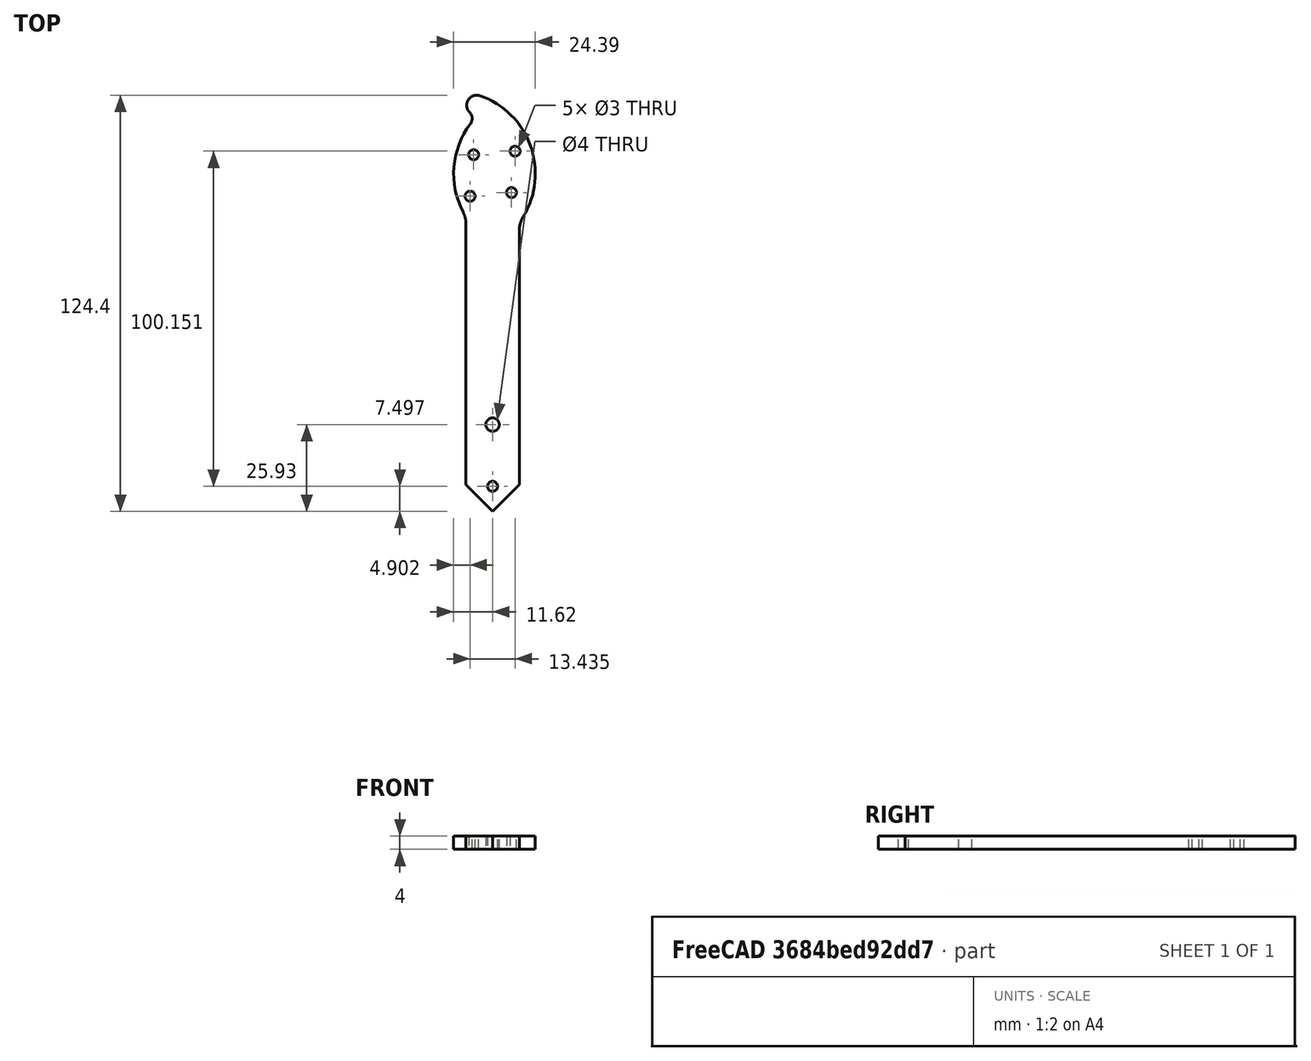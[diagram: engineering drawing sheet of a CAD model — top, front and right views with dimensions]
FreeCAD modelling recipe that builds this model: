
FCSTD DOCUMENT  (FreeCAD 0.18RUnknown)
Label: arm_left
License: All rights reserved
LicenseURL: http://en.wikipedia.org/wiki/All_rights_reserved
objects: Sketcher::SketchObject×1, Part::Extrusion×1, App::Part×1
note: 2 computed .brp shape members not serialized (recipe doc carries the construction recipe); baked Part::Feature solids carry a one-line shape summary decoded from their .brp

FEATURE [Sketcher::SketchObject] Sketch002
  expr: Constraints[9] = anomaly#Spreadsheet.armLength
  expr: Constraints[20] = anomaly#Spreadsheet.armOffsetElectro
  expr: Constraints[10] = anomaly#Spreadsheet.armHoleCenterOffset
  sketch-geometry (24):
    g0: LineSegment StartX=-8 StartY=-92.9332 StartZ=0 EndX=-8 EndY=-17.0009 EndZ=0
    g1: ArcOfCircle CenterX=-16 CenterY=-17.0009 CenterZ=0 NormalX=0 NormalY=0 NormalZ=1 AngleXU=0 Radius=8 StartAngle=-1.039e-13 EndAngle=0.546741
    g2: ArcOfCircle CenterX=15 CenterY=-14.7043 CenterZ=0 NormalX=0 NormalY=0 NormalZ=1 AngleXU=0 Radius=7 StartAngle=2.65925 EndAngle=3.14159
    g3: Circle [constr] CenterX=0 CenterY=0 CenterZ=0 NormalX=0 NormalY=0 NormalZ=1 AngleXU=0 Radius=8
    g4: Circle [constr] CenterX=0 CenterY=0 CenterZ=0 NormalX=0 NormalY=0 NormalZ=1 AngleXU=0 Radius=9.5
    g5: LineSegment [constr] StartX=-6.71751 StartY=6.71751 StartZ=0 EndX=6.71751 EndY=-6.71751 EndZ=0
    g6: LineSegment [constr] StartX=-5.65685 StartY=-5.65685 StartZ=0 EndX=5.65685 EndY=5.65685 EndZ=0
    g7: Circle CenterX=0 CenterY=-75 CenterZ=0 NormalX=0 NormalY=0 NormalZ=1 AngleXU=0 Radius=2
    g8: ArcOfCircle CenterX=11.9331 CenterY=0 CenterZ=0 NormalX=0 NormalY=0 NormalZ=1 AngleXU=0 Radius=24.7 StartAngle=1.90923 EndAngle=3.68833
    g9: ArcOfCircle CenterX=4.72855 CenterY=20.4691 CenterZ=0 NormalX=0 NormalY=0 NormalZ=1 AngleXU=0 Radius=3 StartAngle=5.51344 EndAngle=8.19241
    g10: ArcOfCircle CenterX=8.84318 CenterY=16.4813 CenterZ=0 NormalX=0 NormalY=0 NormalZ=1 AngleXU=0 Radius=2.73 StartAngle=2.37184 EndAngle=3.78616
    g11: ArcOfCircle CenterX=-13.0833 CenterY=0 CenterZ=0 NormalX=0 NormalY=0 NormalZ=1 AngleXU=0 Radius=24.7 StartAngle=5.80084 EndAngle=6.92775
    g12: LineSegment StartX=8 StartY=-42.3168 StartZ=0 EndX=8 EndY=-92.9332 EndZ=0
    g13: Circle CenterX=0 CenterY=-93.4332 CenterZ=0 NormalX=0 NormalY=0 NormalZ=1 AngleXU=0 Radius=1.5
    g14: LineSegment StartX=8 StartY=-14.7043 StartZ=0 EndX=8 EndY=-42.3168 EndZ=0
    g15: LineSegment [constr] StartX=-2 StartY=-115 StartZ=0 EndX=2.32235 EndY=-115 EndZ=0
    g16: LineSegment StartX=-8 StartY=-92.9332 StartZ=0 EndX=0 EndY=-100.933 EndZ=0
    g17: LineSegment StartX=0 StartY=-100.933 StartZ=0 EndX=8 EndY=-92.9332 EndZ=0
    g18: LineSegment [constr] StartX=-8 StartY=-75 StartZ=0 EndX=8 EndY=-75 EndZ=0
    g19: LineSegment [constr] StartX=8 StartY=-42.3168 StartZ=0 EndX=-8 EndY=-42.3168 EndZ=0
    g20: Circle CenterX=6.71751 CenterY=-6.71751 CenterZ=0 NormalX=0 NormalY=0 NormalZ=1 AngleXU=0 Radius=1.5
    g21: Circle CenterX=-5.65685 CenterY=-5.65685 CenterZ=0 NormalX=0 NormalY=0 NormalZ=1 AngleXU=0 Radius=1.5
    g22: Circle CenterX=-6.71751 CenterY=6.71751 CenterZ=0 NormalX=0 NormalY=0 NormalZ=1 AngleXU=0 Radius=1.5
    g23: Circle CenterX=5.65685 CenterY=5.65685 CenterZ=0 NormalX=0 NormalY=0 NormalZ=1 AngleXU=0 Radius=1.5
  constraints (66):
    c: PointOnObject(g3,g-1)
    c: Radius(g3) = 8
    c: PointOnObject(g4,g-1)
    c: Radius(g4) = 9.5
    c: PointOnObject(g4,g-2)
    c: PointOnObject(g3,g-2)
    c: Angle(g5,g6) = 1.5708
    c: PointOnObject(g7,g-2)
    c: DistanceX(g0,g12) = 16
    c: DistanceY(g15,g-1) = 115
    c: DistanceY(g15,g7) = 40
    c: Tangent(g9,g8) = -1.5708
    c: Tangent(g8,g1) = 1.5708
    c: Tangent(g10,g9) = 1.5708
    c: Tangent(g11,g10) = 1.5708
    c: Vertical(g12)
    c: Tangent(g2,g11) = 1.5708
    c: PointOnObject(g8,g-1)
    c: PointOnObject(g11,g-1)
    c: PointOnObject(g13,g-2)
    c: DistanceY(g15,g13) = 21.5668
    c: Radius(g13) = 1.5
    c: DistanceX(g9) = 4.72855
    c: DistanceY(g9) = 20.4691
    c: Coincident(g14,g12)
    c: Horizontal(g15)
    c: Coincident(g16,g0)
    c: PointOnObject(g16,g-2)
    c: Coincident(g17,g16)
    c: Coincident(g17,g12)
    c: Radius(g8) = 24.7
    c: Radius(g9) = 3
    c: PointOnObject(g18,g0)
    c: PointOnObject(g18,g12)
    c: Horizontal(g18)
    c: Symmetric(g18,g18,g7)
    c: PointOnObject(g-1,g5)
    c: PointOnObject(g-1,g6)
    c: PointOnObject(g6,g3)
    c: PointOnObject(g6,g3)
    c: PointOnObject(g5,g4)
    c: PointOnObject(g5,g4)
    c: Angle(g6,g-1) = 2.35619
    c: Radius(g2) = 7
    c: Coincident(g19,g12)
    c: PointOnObject(g19,g0)
    c: Symmetric(g19,g12,g-2)
    c: Tangent(g0,g1) = -1.5708
    c: Radius(g1) = 8
    c: Perpendicular(g17,g16)
    c: Equal(g16,g17)
    c: DistanceY(g16,g13) = 7.5
    c: DistanceY(g2) = -11.4573
    c: Radius(g10) = 2.73
    c: Radius(g11) = 24.7
    c: Radius(g7) = 2
    c: Coincident(g20,g5)
    c: Coincident(g21,g6)
    c: Coincident(g22,g5)
    c: Coincident(g23,g6)
    c: Equal(g23,g20)
    c: Equal(g20,g21)
    c: Equal(g21,g22)
    c: Radius(g20) = 1.5
    c: Tangent(g14,g2) = -1.5708
    c: Vertical(g14)
FEATURE [Part::Extrusion] Extrude001
  Base = -> Sketch002
  Dir = (0,0,1)
  DirMode = 2
  FaceMakerClass = Part::FaceMakerBullseye
  LengthFwd = 0
  LengthRev = 4
  Placement = pos=(0,0,0) rot=(0,1,0;3.14159rad)
  Solid = true
  Symmetric = false
FEATURE [App::Part] Part  label="Arm"
  Group = -> [Extrude001,Sketch002]
  License = CC BY 3.0
  LicenseURL = http://creativecommons.org/licenses/by/3.0/
  Origin = -> Origin
